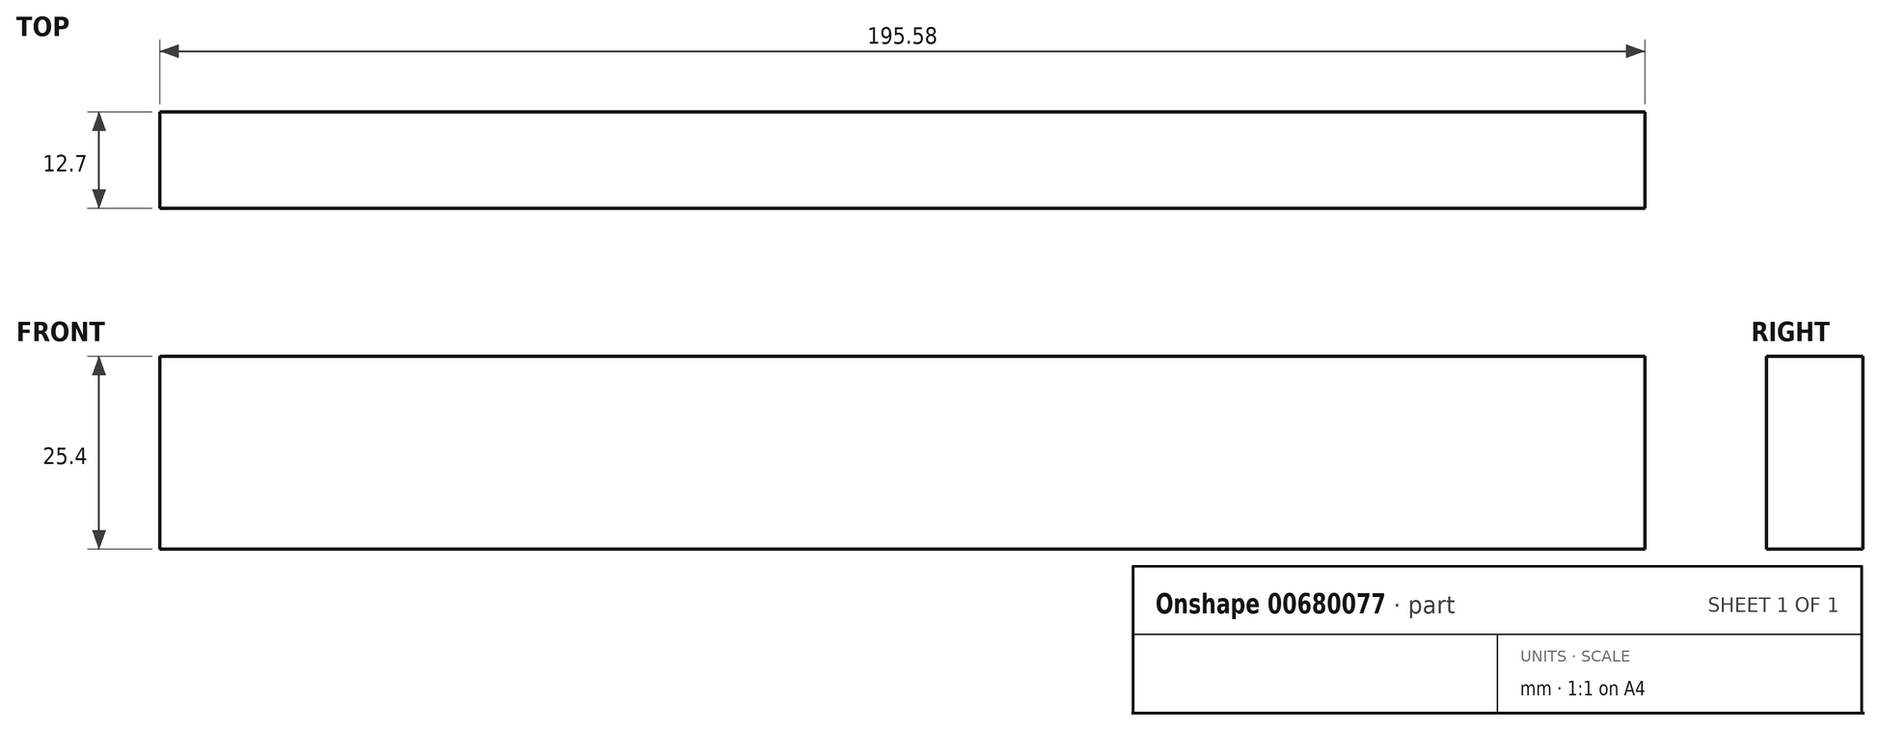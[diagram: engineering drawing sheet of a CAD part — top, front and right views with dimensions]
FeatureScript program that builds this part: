
annotation { "Feature Type Name" : "Feature", "Feature Type Description" : "" }
export const myFeature = defineFeature(function(context is Context, id is Id, definition is map)
    precondition{}
    {
        {
            var Q0;
            Q0=qCreatedBy(makeId("Front.planeOp"),FACE);
            var sketch = newSketch(context, id + "F0", { "sketchPlane" : qUnion([Q0])});
            skLineSegment(sketch, "E0.bottom", {"start": v(-97.8, 12.7) * mm, "end": v(97.8, 12.7) * mm});
            skLineSegment(sketch, "E0.top", {"start": v(-97.8, -12.7) * mm, "end": v(97.8, -12.7) * mm});
            skLineSegment(sketch, "E0.left", {"start": v(-97.8, 12.7) * mm, "end": v(-97.8, -12.7) * mm});
            skLineSegment(sketch, "E0.right", {"start": v(97.8, 12.7) * mm, "end": v(97.8, -12.7) * mm});
            skPoint(sketch, "E0.middle", {"position": v(0, 0) * mm});
            skSolve(sketch);
        }
        {
            var Q0;
            Q0=makeQuery(id+"F0.imprint","IMPRINT",FACE,{"disambiguationData":[TD([[makeQuery(id+"F0.imprint","IMPRINT",EDGE,{"derivedFrom":sQuery(id+"F0.wireOp",EDGE,"E0.bottom")}),-1.0]])]});
            extrude(context, id + "F1", {"entities" : qUnion([Q0]), "depth" : 12.7 * mm, "offsetDistance" : 25.4 * mm});
        }
    });
